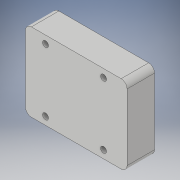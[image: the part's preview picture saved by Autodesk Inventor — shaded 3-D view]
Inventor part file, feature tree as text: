
AUTODESK INVENTOR PART (.ipt)
format: ipt  version: 2019 (Build 230136000, 136)  size: 116,224 bytes
history: native  units: in
note: dims shown in document units (in); Inventor stores cm internally (conversion verified against a paired STEP export)
features: sketch x2, extrude x1, hole x1, fillet x1
ambient origin geometry x8: Origin, YZ Plane, XZ Plane, XY Plane, X Axis, Y Axis, Z Axis, Center Point
bodies: Solid1 (feature_tree)
feature tree (5):
  extrude  "Extrusion1"  Depth=1.651in
  hole  "Hole1"  [1 undecoded]
  fillet  "Fillet1"  Radius=0.165in
  sketch  "Sketch1"  dims[d0=2.145in d1=1.651in]
  sketch  "Sketch2"  dims[d2=0.58in d3=0.0in d4=0.424in d5=0.165in d6=0.496in d7=0.165in d8=0.125in d9=0.75in d10=0.375in d11=0.25in d12=0.5635in d13=1.0in d14=0.8108in d15=0.125in d16=0.166in d17=0.496in d18=0.165in d19=0.424in]
note: 1 required parameter value undecoded (feature->parameter linkage not recoverable at this tier; creation-order binding heuristic only, values carry confidence <= 0.55)
